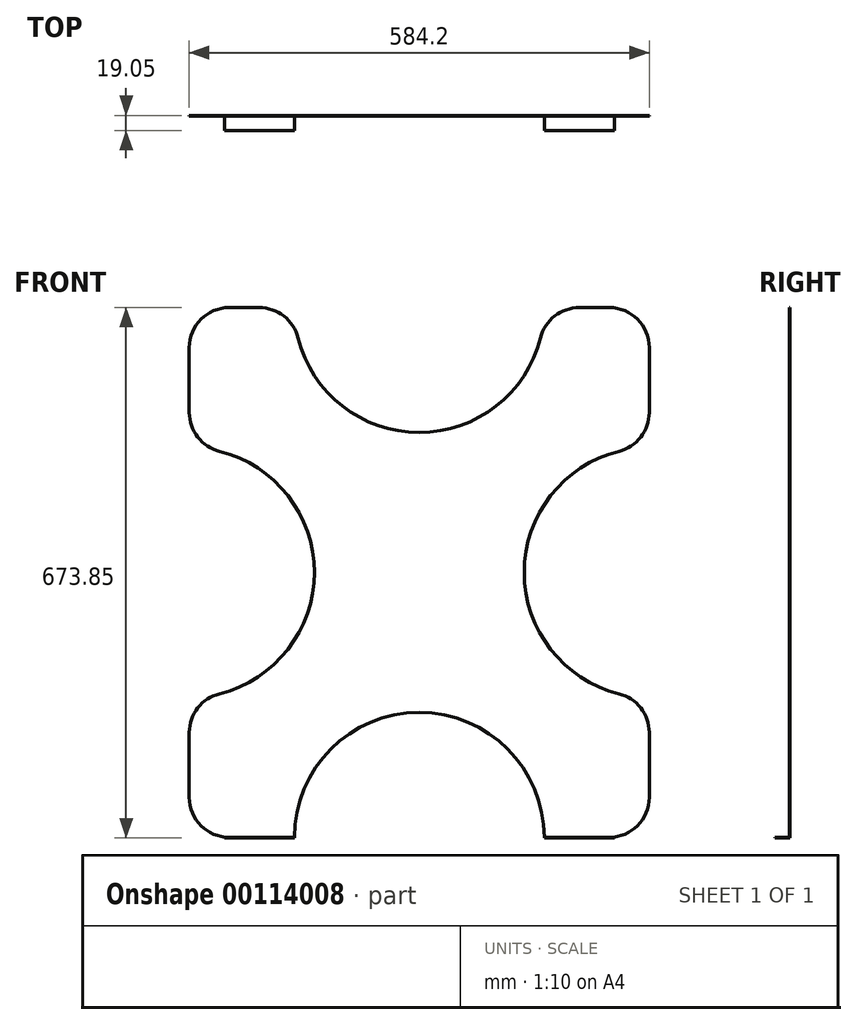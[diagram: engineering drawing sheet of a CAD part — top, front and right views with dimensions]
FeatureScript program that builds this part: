
annotation { "Feature Type Name" : "Feature", "Feature Type Description" : "" }
export const myFeature = defineFeature(function(context is Context, id is Id, definition is map)
    precondition{}
    {
        {
            assignVariable(context, id + "F0", {"name" : "thickness", "anyValue" : 3 / 4});
        }
        {
            var Q0;
            Q0=qCreatedBy(makeId("Front.planeOp"),FACE);
            var sketch = newSketch(context, id + "F1", { "sketchPlane" : qUnion([Q0])});
            skLineSegment(sketch, "E0.bottom", {"start": v(-292.1, 336.55) * mm, "end": v(292.1, 336.55) * mm});
            skLineSegment(sketch, "E0.top", {"start": v(-292.1, -336.55) * mm, "end": v(292.1, -336.55) * mm});
            skLineSegment(sketch, "E0.left", {"start": v(-292.1, 336.55) * mm, "end": v(-292.1, -336.55) * mm});
            skLineSegment(sketch, "E0.right", {"start": v(292.1, 336.55) * mm, "end": v(292.1, -336.55) * mm});
            skPoint(sketch, "E1", {"position": v(0, 336.55) * mm});
            skPoint(sketch, "E2", {"position": v(-292.1, 0) * mm});
            skLineSegment(sketch, "E3", {"start": v(0, 0) * mm, "end": v(-292.1, 0) * mm, "construction": true});
            skLineSegment(sketch, "E4", {"start": v(0, 0) * mm, "end": v(0, 336.55) * mm, "construction": true});
            skCircle(sketch, "E5", {"center": v(-292.1, 0) * mm, "radius": 158.75 * mm});
            skCircle(sketch, "E6.MirrorC", {"center": v(292.1, 0) * mm, "radius": 158.75 * mm});
            skCircle(sketch, "E7", {"center": v(0, 336.55) * mm, "radius": 158.75 * mm});
            skCircle(sketch, "E8.MirrorC", {"center": v(0, -336.55) * mm, "radius": 158.75 * mm});
            skSolve(sketch);
        }
        {
            var Q0;
            {var subQ4=sQuery(id+"F1.wireOp",EDGE,"E0.left");var subQ11=sQuery(id+"F1.wireOp",EDGE,"E0.bottom");var subQ12=makeQuery(id+"F1.imprint","INTERSECT",VERTEX,{"derivedFrom":[subQ11,subQ4]});Q0=makeQuery(id+"F1.imprint","IMPRINT",FACE,{"disambiguationData":[TD([[makeQuery(id+"F1.imprint","IMPRINT",EDGE,{"disambiguationData":[TD([[subQ12,-1.0]])],"derivedFrom":subQ11}),-1.0]])]});}
            extrude(context, id + "F2", {"entities" : qUnion([Q0]), "depth" : (getVariable(context, 'thickness')) * mm});
        }
        {
            var Q0;
            {var subQ0=sQuery(id+"F1.wireOp",EDGE,"E7");var subQ1=sQuery(id+"F1.wireOp",EDGE,"E0.bottom");Q0=makeQuery(id+"F2.opExtrude","SWEPT_EDGE",EDGE,{"disambiguationData":[OSD([subQ1,subQ0]),TDD([makeQuery(id+"F1.imprint","INTERSECT",VERTEX,{"disambiguationData":[OD(1.0)],"derivedFrom":[subQ1,subQ0]})])]});}
            var Q1;
            {var subQ0=sQuery(id+"F1.wireOp",EDGE,"E7");var subQ1=sQuery(id+"F1.wireOp",EDGE,"E0.bottom");Q1=makeQuery(id+"F2.opExtrude","SWEPT_EDGE",EDGE,{"disambiguationData":[OSD([subQ1,subQ0]),TDD([makeQuery(id+"F1.imprint","INTERSECT",VERTEX,{"disambiguationData":[OD(0.0)],"derivedFrom":[subQ1,subQ0]})])]});}
            var Q2;
            {var subQ0=sQuery(id+"F1.wireOp",EDGE,"E6.MirrorC");var subQ1=sQuery(id+"F1.wireOp",EDGE,"E0.right");Q2=makeQuery(id+"F2.opExtrude","SWEPT_EDGE",EDGE,{"disambiguationData":[OSD([subQ1,subQ0]),TDD([makeQuery(id+"F1.imprint","INTERSECT",VERTEX,{"disambiguationData":[OD(0.0)],"derivedFrom":[subQ1,subQ0]})])]});}
            var Q3;
            {var subQ0=sQuery(id+"F1.wireOp",EDGE,"E6.MirrorC");var subQ1=sQuery(id+"F1.wireOp",EDGE,"E0.right");Q3=makeQuery(id+"F2.opExtrude","SWEPT_EDGE",EDGE,{"disambiguationData":[OSD([subQ1,subQ0]),TDD([makeQuery(id+"F1.imprint","INTERSECT",VERTEX,{"disambiguationData":[OD(1.0)],"derivedFrom":[subQ1,subQ0]})])]});}
            var Q4;
            {var subQ0=sQuery(id+"F1.wireOp",EDGE,"E5");var subQ1=sQuery(id+"F1.wireOp",EDGE,"E0.left");Q4=makeQuery(id+"F2.opExtrude","SWEPT_EDGE",EDGE,{"disambiguationData":[OSD([subQ1,subQ0]),TDD([makeQuery(id+"F1.imprint","INTERSECT",VERTEX,{"disambiguationData":[OD(1.0)],"derivedFrom":[subQ1,subQ0]})])]});}
            var Q5;
            {var subQ0=sQuery(id+"F1.wireOp",EDGE,"E5");var subQ1=sQuery(id+"F1.wireOp",EDGE,"E0.left");Q5=makeQuery(id+"F2.opExtrude","SWEPT_EDGE",EDGE,{"disambiguationData":[OSD([subQ1,subQ0]),TDD([makeQuery(id+"F1.imprint","INTERSECT",VERTEX,{"disambiguationData":[OD(0.0)],"derivedFrom":[subQ1,subQ0]})])]});}
            var Q6;
            Q6=makeQuery(id+"F2.opExtrude","SWEPT_EDGE",EDGE,{"disambiguationData":[OSD([sQuery(id+"F1.wireOp",EDGE,"E0.top"),sQuery(id+"F1.wireOp",EDGE,"E0.right")])]});
            var Q7;
            Q7=makeQuery(id+"F2.opExtrude","SWEPT_EDGE",EDGE,{"disambiguationData":[OSD([sQuery(id+"F1.wireOp",EDGE,"E0.top"),sQuery(id+"F1.wireOp",EDGE,"E0.left")])]});
            var Q8;
            Q8=makeQuery(id+"F2.opExtrude","SWEPT_EDGE",EDGE,{"disambiguationData":[OSD([sQuery(id+"F1.wireOp",EDGE,"E0.bottom"),sQuery(id+"F1.wireOp",EDGE,"E0.right")])]});
            var Q9;
            Q9=makeQuery(id+"F2.opExtrude","SWEPT_EDGE",EDGE,{"disambiguationData":[OSD([sQuery(id+"F1.wireOp",EDGE,"E0.bottom"),sQuery(id+"F1.wireOp",EDGE,"E0.left")])]});
            fillet(context, id + "F3", {"entities" : qUnion([Q0, Q1, Q2, Q3, Q4, Q5, Q6, Q7, Q8, Q9]), "radius" : 50.8 * mm, "tangentPropagation" : true, "allowEdgeOverflow" : false});
        }
        {
            var Q0;
            {var subQ0=sQuery(id+"F1.wireOp",EDGE,"E0.top");Q0=makeQuery(id+"F2.opExtrude","SWEPT_FACE",FACE,{"disambiguationData":[OSD([subQ0]),TDD([makeQuery(id+"F1.imprint","IMPRINT",EDGE,{"disambiguationData":[TD([[makeQuery(id+"F1.imprint","INTERSECT",VERTEX,{"derivedFrom":[subQ0,sQuery(id+"F1.wireOp",EDGE,"E0.left")]}),-1.0]])],"derivedFrom":subQ0})])]});}
            var sketch = newSketch(context, id + "F4", { "sketchPlane" : qUnion([Q0])});
            skLineSegment(sketch, "E9.bottom", {"start": v(-158.75, 19.05) * mm, "end": v(-247.65, 19.05) * mm});
            skLineSegment(sketch, "E9.top", {"start": v(-158.75, 0) * mm, "end": v(-247.65, 0) * mm});
            skLineSegment(sketch, "E9.left", {"start": v(-158.75, 19.05) * mm, "end": v(-158.75, 0) * mm});
            skLineSegment(sketch, "E9.right", {"start": v(-247.65, 19.05) * mm, "end": v(-247.65, 0) * mm});
            skLineSegment(sketch, "E10.bottom", {"start": v(158.75, 19.05) * mm, "end": v(247.65, 19.05) * mm});
            skLineSegment(sketch, "E10.top", {"start": v(158.75, 0) * mm, "end": v(247.65, 0) * mm});
            skLineSegment(sketch, "E10.left", {"start": v(158.75, 19.05) * mm, "end": v(158.75, 0) * mm});
            skLineSegment(sketch, "E10.right", {"start": v(247.65, 19.05) * mm, "end": v(247.65, 0) * mm});
            skSolve(sketch);
        }
        {
            var Q0;
            Q0=qSketchRegion(id+"F4",true);
            extrude(context, id + "F5", {"entities" : qUnion([Q0]), "operationType" : NewBodyOperationType.ADD, "depth" : (getVariable(context, 'thickness')) * mm});
        }
    });
